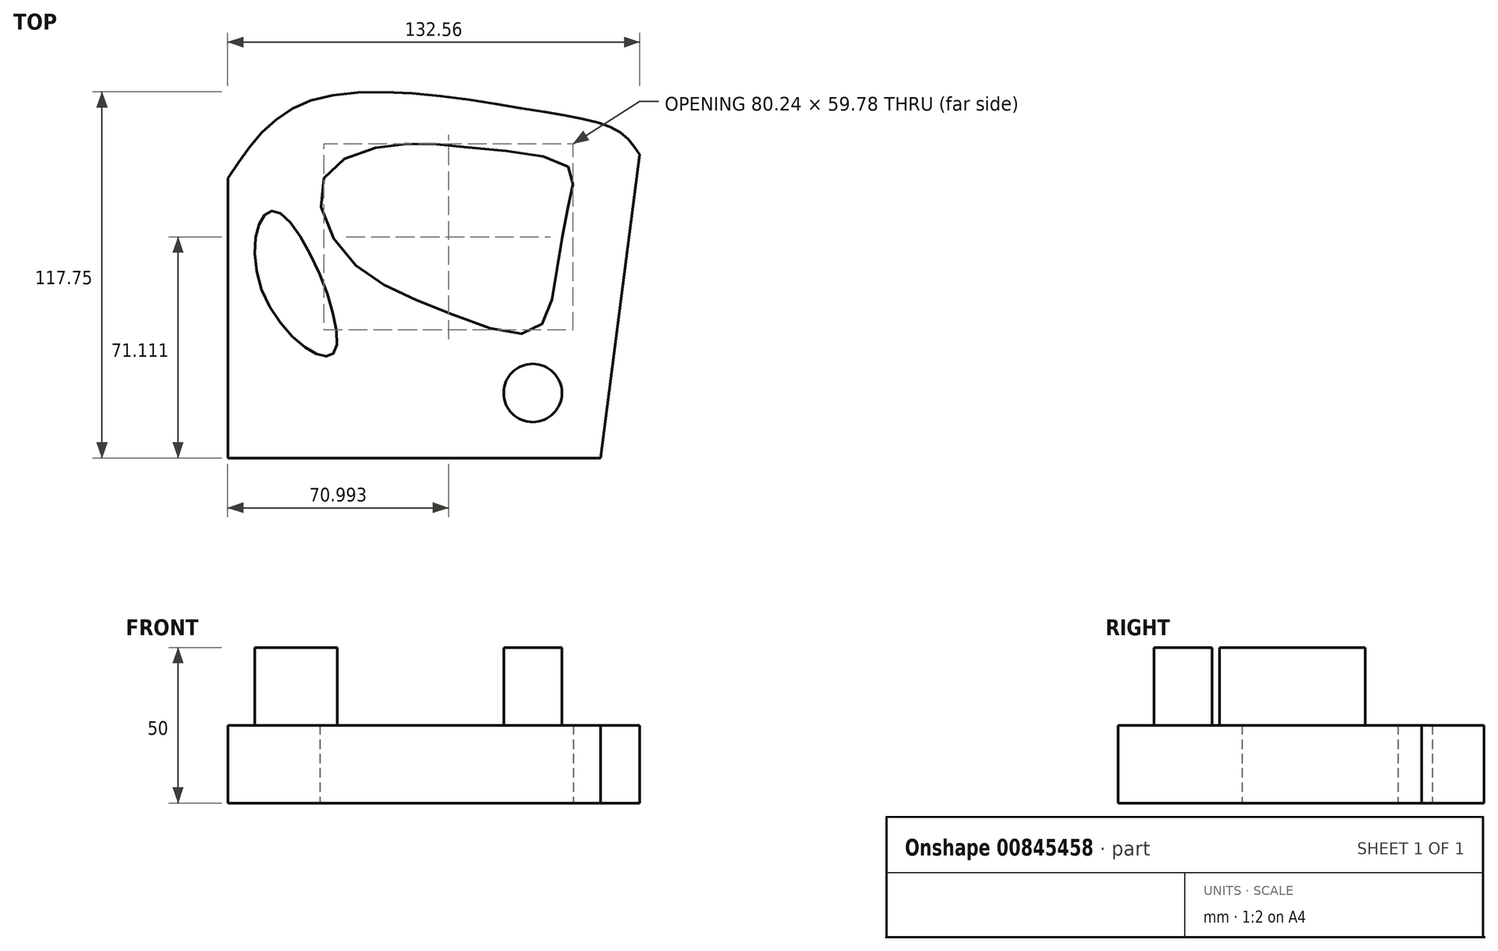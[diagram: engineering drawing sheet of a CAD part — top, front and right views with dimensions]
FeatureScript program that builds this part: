
annotation { "Feature Type Name" : "Feature", "Feature Type Description" : "" }
export const myFeature = defineFeature(function(context is Context, id is Id, definition is map)
    precondition{}
    {
        {
            var Q0;
            Q0=qCreatedBy(makeId("Top.planeOp"),FACE);
            var sketch = newSketch(context, id + "F0", { "sketchPlane" : qUnion([Q0])});
            skLineSegment(sketch, "E0", {"start": v(-79.39, 49.25) * mm, "end": v(-79.39, -40.75) * mm});
            skLineSegment(sketch, "E1", {"start": v(40.61, -40.75) * mm, "end": v(-79.39, -40.75) * mm});
            skLineSegment(sketch, "E2", {"start": v(53.17, 56.92) * mm, "end": v(40.61, -40.75) * mm});
            skFitSpline(sketch, "E3", {"points": [v(-79.39, 49.25) * mm, v(-51.9, 74.45) * mm, v(19.31, 71.06) * mm, v(46.44, 64.27) * mm, v(53.17, 56.92) * mm], "startDerivative": vector(78.4, 118.07) * mm, "endDerivative": vector(39.53, -58.78) * mm});
            skSolve(sketch);
        }
        {
            var Q0;
            Q0=makeQuery(id+"F0.imprint","IMPRINT",FACE,{"disambiguationData":[TD([[makeQuery(id+"F0.imprint","IMPRINT",EDGE,{"derivedFrom":sQuery(id+"F0.wireOp",EDGE,"E0")}),1.0]])]});
            extrude(context, id + "F1", {"entities" : qUnion([Q0]), "depth" : 25 * mm, "offsetDistance" : 25 * mm});
        }
        {
            var Q0;
            Q0=makeQuery(id+"F1.opExtrude","CAP_FACE",FACE,{"disambiguationData":[OSD([sQuery(id+"F0.wireOp",EDGE,"E0"),sQuery(id+"F0.wireOp",EDGE,"E1"),sQuery(id+"F0.wireOp",EDGE,"E2"),sQuery(id+"F0.wireOp",EDGE,"e002d61e-a04e-4640-b456-309efe5fb611")])],"isStart":false});
            var sketch = newSketch(context, id + "F2", { "sketchPlane" : qUnion([Q0])});
            skFitSpline(sketch, "E4", {"points": [v(-68.5, 13.48) * mm, v(-63.6, 38.47) * mm, v(-44.97, -6.62) * mm, v(-68.5, 13.48) * mm]});
            skCircle(sketch, "E5", {"center": v(18.75, -19.85) * mm, "radius": 9.36 * mm});
            skSolve(sketch);
        }
        {
            var Q0;
            Q0 = qSketchRegion(id + "F2", true);
            extrude(context, id + "F3", {"entities" : qUnion([Q0]), "operationType" : NewBodyOperationType.ADD, "depth" : 25 * mm, "offsetDistance" : 25 * mm});
        }
        {
            var Q0;
            Q0=makeQuery(id+"F1.opExtrude","CAP_FACE",FACE,{"disambiguationData":[OSD([sQuery(id+"F0.wireOp",EDGE,"E0"),sQuery(id+"F0.wireOp",EDGE,"E1"),sQuery(id+"F0.wireOp",EDGE,"E2"),sQuery(id+"F0.wireOp",EDGE,"E3")])],"isStart":false});
            var sketch = newSketch(context, id + "F4", { "sketchPlane" : qUnion([Q0])});
            skFitSpline(sketch, "E6", {"points": [v(-48.52, 49.2) * mm, v(-41.08, 24.05) * mm, v(-11.3, 7.11) * mm, v(18.98, 0) * mm, v(26.16, 17.38) * mm, v(30.53, 42.01) * mm, v(30.27, 52.8) * mm, v(0, 58.95) * mm, v(-25.93, 59.98) * mm, v(-48.52, 49.2) * mm]});
            skSolve(sketch);
        }
        {
            var Q0;
            Q0 = qSketchRegion(id + "F4", true);
            extrude(context, id + "F5", {"entities" : qUnion([Q0]), "operationType" : NewBodyOperationType.REMOVE, "endBound" : BoundingType.THROUGH_ALL, "oppositeDirection" : true, "depth" : 25 * mm, "offsetDistance" : 25 * mm});
        }
    });
